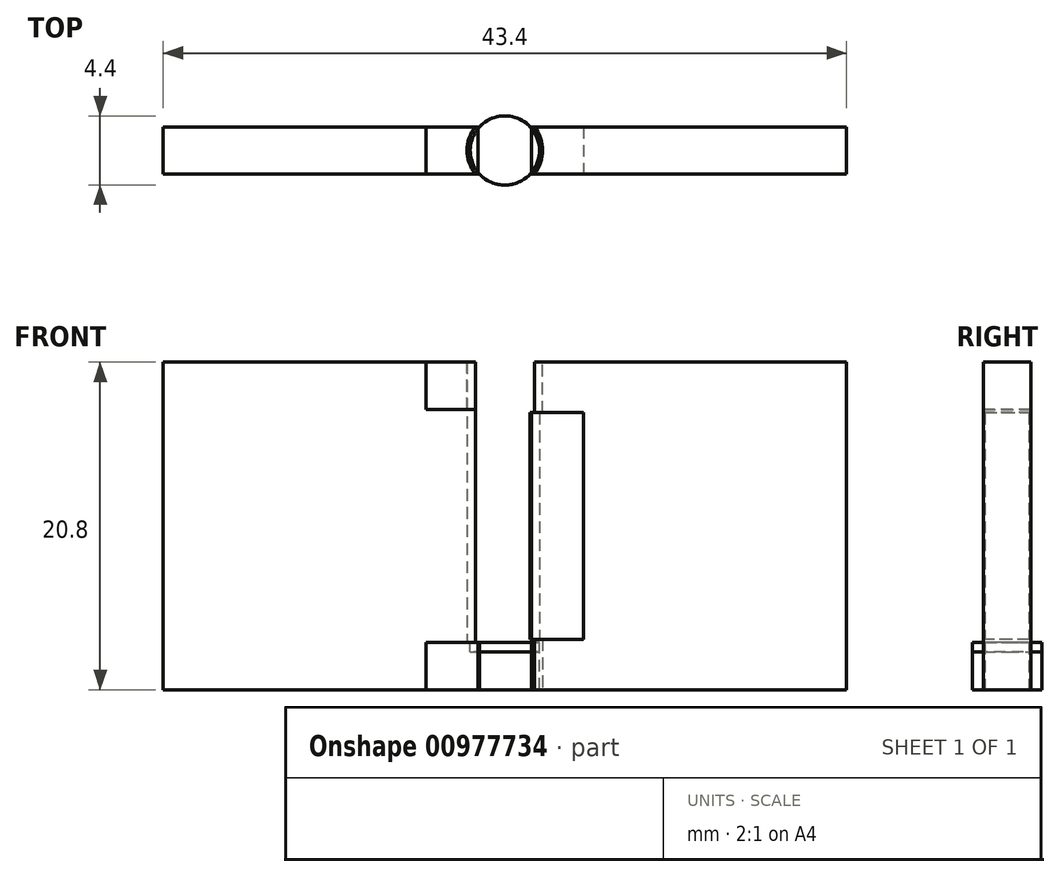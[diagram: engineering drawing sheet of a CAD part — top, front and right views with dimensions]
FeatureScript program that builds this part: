
annotation { "Feature Type Name" : "Feature", "Feature Type Description" : "" }
export const myFeature = defineFeature(function(context is Context, id is Id, definition is map)
    precondition{}
    {
        {
            var Q0;
            Q0=qCreatedBy(makeId("Front.planeOp"),FACE);
            var sketch = newSketch(context, id + "F0", { "sketchPlane" : qUnion([Q0])});
            skLineSegment(sketch, "E0", {"start": v(-1, 0.6) * mm, "end": v(-1, 2.6) * mm});
            skLineSegment(sketch, "E1", {"start": v(-1, 13.4) * mm, "end": v(-1, 15.4) * mm});
            skLineSegment(sketch, "E2", {"start": v(0, 20) * mm, "end": v(0, 0) * mm});
            skFitSpline(sketch, "E3", {"points": [v(-1, 13.4) * mm, v(-1, 2.6) * mm], "startDerivative": vector(2.12, -2.12) * mm, "endDerivative": vector(-2.12, -2.12) * mm});
            skLineSegment(sketch, "E4", {"start": v(-1, 13.4) * mm, "end": v(-0.3, 12.7) * mm, "construction": true});
            skLineSegment(sketch, "E5", {"start": v(-1, 2.6) * mm, "end": v(-0.3, 3.3) * mm, "construction": true});
            skLineSegment(sketch, "E6", {"start": v(-1.2, 15.2) * mm, "end": v(-1.2, 13.32) * mm});
            skLineSegment(sketch, "E7", {"start": v(-1.2, 2.68) * mm, "end": v(-1.2, 0.8) * mm});
            skFitSpline(sketch, "E8", {"points": [v(-1.2, 13.32) * mm, v(-1.2, 2.68) * mm], "startDerivative": vector(2.12, -2.12) * mm, "endDerivative": vector(-2.12, -2.12) * mm});
            skLineSegment(sketch, "E9", {"start": v(-1.2, 2.68) * mm, "end": v(-0.5, 3.39) * mm, "construction": true});
            skLineSegment(sketch, "E10", {"start": v(-1.2, 13.32) * mm, "end": v(-0.5, 12.61) * mm, "construction": true});
            skLineSegment(sketch, "E11", {"start": v(-1.2, 15.2) * mm, "end": v(-2.2, 15.2) * mm});
            skLineSegment(sketch, "E12", {"start": v(-2.2, 15.2) * mm, "end": v(-2.2, 0.8) * mm});
            skLineSegment(sketch, "E13", {"start": v(-2.2, 0.8) * mm, "end": v(-1.2, 0.8) * mm});
            skLineSegment(sketch, "E14", {"start": v(-1, 15.4) * mm, "end": v(-2.2, 15.4) * mm});
            skLineSegment(sketch, "E15", {"start": v(-2.2, 15.4) * mm, "end": v(-2.2, 16) * mm});
            skLineSegment(sketch, "E16", {"start": v(-2.2, 16) * mm, "end": v(0, 16) * mm});
            skLineSegment(sketch, "E17", {"start": v(0, 20) * mm, "end": v(0, 16) * mm});
            skLineSegment(sketch, "E18", {"start": v(-1, 0.6) * mm, "end": v(-2.2, 0.6) * mm});
            skLineSegment(sketch, "E19", {"start": v(-2.2, 0.6) * mm, "end": v(-2.2, 0) * mm});
            skLineSegment(sketch, "E20", {"start": v(-2.2, 0) * mm, "end": v(0, 0) * mm});
            skPoint(sketch, "E21", {"position": v(-2.2, 8) * mm});
            skSolve(sketch);
        }
        {
            var Q0;
            {Q0=qUnion([makeQuery(id+"F0.imprint","IMPRINT",FACE,{"disambiguationData":[TD([[makeQuery(id+"F0.imprint","IMPRINT",EDGE,{"derivedFrom":sQuery(id+"F0.wireOp",EDGE,"E0")}),-1.0]])]}),makeQuery(id+"F0.imprint","IMPRINT",FACE,{"disambiguationData":[TD([[makeQuery(id+"F0.imprint","IMPRINT",EDGE,{"derivedFrom":sQuery(id+"F0.wireOp",EDGE,"E6")}),-1.0]])]})]);}
            var Q1;
            Q1=sQuery(id+"F0.wireOp",EDGE,"E2");
            revolve(context, id + "F1", {"surfaceOperationType" : NewSurfaceOperationType.NEW, "entities" : qUnion([Q0]), "axis" : qUnion([Q1]), "revolveType" : RevolveType.FULL});
        }
        {
            var Q0;
            Q0=makeQuery(id+"F1.opRevolve","SWEPT_FACE",FACE,{"disambiguationData":[OSD([sQuery(id+"F0.wireOp",EDGE,"E14")])]});
            var sketch = newSketch(context, id + "F2", { "sketchPlane" : qUnion([Q0])});
            skCircle(sketch, "E22.0", {"center": v(0, 0) * mm, "radius": 2.2 * mm});
            skLineSegment(sketch, "E23", {"start": v(-5, -1.5) * mm, "end": v(-5, 1.5) * mm});
            skPoint(sketch, "E24", {"position": v(-5, 0) * mm});
            skLineSegment(sketch, "E25", {"start": v(-5, 1.5) * mm, "end": v(-1.6, 1.5) * mm});
            skLineSegment(sketch, "E26", {"start": v(-5, -1.5) * mm, "end": v(-1.6, -1.5) * mm});
            skSolve(sketch);
        }
        {
            var Q0;
            Q0=qSketchRegion(id+"F2",true);
            extrude(context, id + "F3", {"entities" : qUnion([Q0]), "oppositeDirection" : true, "depth" : 3 * mm, "offsetDistance" : 25 * mm});
        }
        {
            var Q0;
            Q0=sQuery(id+"F0.wireOp",EDGE,"E12");
            cPoint(context, id + "F4", {"entities" : qUnion([Q0]), "parameter" : 0.5});
        }
        {
            var Q0;
            Q0=qCreatedBy(id+"F4",VERTEX);
            var Q1;
            Q1=qCreatedBy(makeId("Top.planeOp"),FACE);
            cPlane(context, id + "F5", {"entities" : qUnion([Q0, Q1]), "cplaneType" : CPlaneType.PLANE_POINT, "offset" : 10 * mm, "oppositeDirection" : true, "width" : 150 * mm, "height" : 150 * mm});
        }
        {
            var Q0;
            Q0=makeQuery(id+"F3.opExtrude","SWEPT_BODY",BODY,{"disambiguationData":[OSD([sQuery(id+"F2.wireOp",EDGE,"E22.0"),sQuery(id+"F2.wireOp",EDGE,"TC6tmQ0S-Yqyp-8cfE-aPuB-eqh3s4vsYZ5D"),sQuery(id+"F2.wireOp",EDGE,"bjhKsaEG-cVOX-Fkbz-CbkF-KtJ3GnmFkV8B"),sQuery(id+"F2.wireOp",EDGE,"mCJQ4lcK-q60s-A4tl-M03E-BbWkXgAuEyKJ")])]});
            var Q1;
            Q1=qCreatedBy(id+"F5.planeOp",FACE);
            mirror(context, id + "F6", {"entities" : qUnion([Q0]), "mirrorPlane" : qUnion([Q1])});
        }
        {
            var Q0;
            Q0=makeQuery(id+"F1.opRevolve","SWEPT_FACE",FACE,{"disambiguationData":[OSD([sQuery(id+"F0.wireOp",EDGE,"E11")])]});
            var sketch = newSketch(context, id + "F7", { "sketchPlane" : qUnion([Q0])});
            skCircle(sketch, "E27.0.0", {"center": v(0, 0) * mm, "radius": 2.2 * mm});
            skCircle(sketch, "E28.0", {"center": v(0, 0) * mm, "radius": 1.2 * mm});
            skLineSegment(sketch, "E29", {"start": v(5, 1.5) * mm, "end": v(5, -1.5) * mm});
            skPoint(sketch, "E30", {"position": v(5, 0) * mm});
            skLineSegment(sketch, "E31", {"start": v(5, -1.5) * mm, "end": v(1.6, -1.5) * mm});
            skLineSegment(sketch, "E32", {"start": v(5, 1.5) * mm, "end": v(1.6, 1.5) * mm});
            skSolve(sketch);
        }
        {
            var Q0;
            Q0=makeQuery(id+"F7.imprint","IMPRINT",FACE,{"disambiguationData":[TD([[makeQuery(id+"F7.imprint","IMPRINT",EDGE,{"derivedFrom":sQuery(id+"F7.wireOp",EDGE,"E29")}),-1.0]])]});
            var Q1;
            Q1=qCreatedBy(id+"F5.planeOp",FACE);
            extrude(context, id + "F8", {"entities" : qUnion([Q0]), "endBound" : BoundingType.UP_TO_SURFACE, "oppositeDirection" : true, "depth" : 6 * mm, "endBoundEntityFace" : qUnion([Q1]), "offsetDistance" : 25 * mm});
        }
        {
            var Q0;
            Q0=makeQuery(id+"F8.opExtrude","SWEPT_BODY",BODY,{"disambiguationData":[OSD([sQuery(id+"F7.wireOp",EDGE,"E27.0.0"),sQuery(id+"F7.wireOp",EDGE,"IGmIIkr0-UC7I-SQ2f-CYrj-rGYYXajgl1JJ"),sQuery(id+"F7.wireOp",EDGE,"ZHcqityA-W586-mcKd-Iscn-xaArEYFfNkmQ"),sQuery(id+"F7.wireOp",EDGE,"cz0Gnaut-MDit-a28b-WmXf-ZYZsQhrKTzKM")])]});
            var Q1;
            Q1=qCreatedBy(id+"F5.planeOp",FACE);
            mirror(context, id + "F9", {"entities" : qUnion([Q0]), "mirrorPlane" : qUnion([Q1])});
        }
        {
            var Q0;
            Q0=makeQuery(id+"F1.opRevolve","SWEPT_BODY",BODY,{"disambiguationData":[OSD([sQuery(id+"F0.wireOp",EDGE,"E6"),sQuery(id+"F0.wireOp",EDGE,"E7"),sQuery(id+"F0.wireOp",EDGE,"E8"),sQuery(id+"F0.wireOp",EDGE,"E11"),sQuery(id+"F0.wireOp",EDGE,"E12"),sQuery(id+"F0.wireOp",EDGE,"E13")])]});
            var Q1;
            Q1=makeQuery(id+"F8.opExtrude","SWEPT_BODY",BODY,{"disambiguationData":[OSD([sQuery(id+"F7.wireOp",EDGE,"E27.0.0"),sQuery(id+"F7.wireOp",EDGE,"IGmIIkr0-UC7I-SQ2f-CYrj-rGYYXajgl1JJ"),sQuery(id+"F7.wireOp",EDGE,"ZHcqityA-W586-mcKd-Iscn-xaArEYFfNkmQ"),sQuery(id+"F7.wireOp",EDGE,"cz0Gnaut-MDit-a28b-WmXf-ZYZsQhrKTzKM")])]});
            var Q2;
            Q2=makeQuery(id+"F9.opPattern","COPY",BODY,{"derivedFrom":makeQuery(id+"F8.opExtrude","SWEPT_BODY",BODY,{"disambiguationData":[OSD([sQuery(id+"F7.wireOp",EDGE,"E27.0.0"),sQuery(id+"F7.wireOp",EDGE,"IGmIIkr0-UC7I-SQ2f-CYrj-rGYYXajgl1JJ"),sQuery(id+"F7.wireOp",EDGE,"ZHcqityA-W586-mcKd-Iscn-xaArEYFfNkmQ"),sQuery(id+"F7.wireOp",EDGE,"cz0Gnaut-MDit-a28b-WmXf-ZYZsQhrKTzKM")])]}),"instanceName":"1"});
            booleanBodies(context, id + "F10", {"operationType" : BooleanOperationType.UNION, "tools" : qUnion([Q0, Q1, Q2])});
        }
        {
            var Q0;
            Q0=qCreatedBy(makeId("Front.planeOp"),FACE);
            var sketch = newSketch(context, id + "F11", { "sketchPlane" : qUnion([Q0])});
            skLineSegment(sketch, "E33", {"start": v(-2.2, 0.8) * mm, "end": v(-2.2, 15.2) * mm});
            skLineSegment(sketch, "E34.bottom", {"start": v(-21.7, 18.4) * mm, "end": v(-1.7, 18.4) * mm});
            skLineSegment(sketch, "E34.top", {"start": v(-21.7, -2.4) * mm, "end": v(-1.7, -2.4) * mm});
            skLineSegment(sketch, "E34.left", {"start": v(-21.7, 18.4) * mm, "end": v(-21.7, -2.4) * mm});
            skLineSegment(sketch, "E34.right", {"start": v(-1.7, 18.4) * mm, "end": v(-1.7, -2.4) * mm});
            skLineSegment(sketch, "E35.bottom", {"start": v(21.7, 18.4) * mm, "end": v(1.7, 18.4) * mm});
            skLineSegment(sketch, "E35.top", {"start": v(21.7, -2.4) * mm, "end": v(1.7, -2.4) * mm});
            skLineSegment(sketch, "E35.left", {"start": v(21.7, 18.4) * mm, "end": v(21.7, -2.4) * mm});
            skLineSegment(sketch, "E35.right", {"start": v(1.7, 18.4) * mm, "end": v(1.7, -2.4) * mm});
            skLineSegment(sketch, "E36.0", {"start": v(-1.6, -2.4) * mm, "end": v(2.2, -2.4) * mm});
            skLineSegment(sketch, "E37.0", {"start": v(-1.6, 18.4) * mm, "end": v(2.2, 18.4) * mm});
            skLineSegment(sketch, "E38.MirrorCS", {"start": v(2.2, 0.8) * mm, "end": v(2.2, 15.2) * mm});
            skSolve(sketch);
        }
        {
            var Q0;
            Q0=qSketchRegion(id+"F11",true);
            extrude(context, id + "F12", {"entities" : qUnion([Q0]), "endBound" : BoundingType.SYMMETRIC, "depth" : 3 * mm, "offsetDistance" : 25 * mm});
        }
        {
            var Q0;
            Q0=makeQuery(id+"F12.opExtrude","SWEPT_FACE",FACE,{"disambiguationData":[OSD([sQuery(id+"F11.wireOp",EDGE,"E35.top")])]});
            var sketch = newSketch(context, id + "F13", { "sketchPlane" : qUnion([Q0])});
            skLineSegment(sketch, "E39.0", {"start": v(1.6, 1.5) * mm, "end": v(1.6, 1.5) * mm});
            skCircle(sketch, "E40", {"center": v(0, 0) * mm, "radius": 2.4 * mm});
            skArc(sketch, "E41.0", {"start": v(-1.6, 1.5) * mm, "mid": v(2.2, 0) * mm, "end": v(-1.6, -1.5) * mm});
            skSolve(sketch);
        }
        {
            var Q0;
            {var subQ0=sQuery(id+"F11.wireOp",EDGE,"E35.top");var subQ6=makeQuery(id+"F12.opExtrude","CAP_EDGE",EDGE,{"disambiguationData":[OSD([subQ0])],"isStart":true});var subQ9=sQuery(id+"F13.wireOp",EDGE,"E40");var subQ10=makeQuery(id+"F13.imprint","INTERSECT",VERTEX,{"derivedFrom":[subQ6,subQ9]});Q0=makeQuery(id+"F13.imprint","IMPRINT",FACE,{"disambiguationData":[TD([[makeQuery(id+"F13.imprint","IMPRINT",EDGE,{"disambiguationData":[TD([[subQ10,-1.0]])],"derivedFrom":subQ9}),1.0]])]});}
            var Q1;
            {var subQ0=sQuery(id+"F13.wireOp",EDGE,"ac114a6b-6946-46ee-80ea-92bb40bdf1b8.0");var subQ1=makeQuery(id+"F12.opExtrude","SWEPT_EDGE",EDGE,{"disambiguationData":[OSD([sQuery(id+"F11.wireOp",EDGE,"E35.top"),sQuery(id+"F11.wireOp",EDGE,"E35.right")])]});var subQ2=makeQuery(id+"F13.imprint","INTERSECT",VERTEX,{"disambiguationData":[OD(0.0)],"derivedFrom":[subQ1,subQ0]});Q1=makeQuery(id+"F13.imprint","IMPRINT",FACE,{"disambiguationData":[TD([[makeQuery(id+"F13.imprint","IMPRINT",EDGE,{"disambiguationData":[TD([[subQ2,-1.0]])],"derivedFrom":subQ0}),-1.0]])]});}
            var Q2;
            {var subQ0=sQuery(id+"F13.wireOp",EDGE,"E41.0");var subQ1=makeQuery(id+"F12.opExtrude","SWEPT_EDGE",EDGE,{"disambiguationData":[OSD([sQuery(id+"F11.wireOp",EDGE,"E35.right"),sQuery(id+"F11.wireOp",EDGE,"E36.0")])]});var subQ2=makeQuery(id+"F13.imprint","INTERSECT",VERTEX,{"disambiguationData":[OD(0.0)],"derivedFrom":[subQ1,subQ0]});Q2=makeQuery(id+"F13.imprint","IMPRINT",FACE,{"disambiguationData":[TD([[makeQuery(id+"F13.imprint","IMPRINT",EDGE,{"disambiguationData":[TD([[subQ2,1.0]])],"derivedFrom":subQ0}),-1.0]])]});}
            var Q3;
            Q3=makeQuery(id+"F10.opBoolean","MERGE",FACE,{"derivedFrom":[makeQuery(id+"F1.opRevolve","SWEPT_FACE",FACE,{"disambiguationData":[OSD([sQuery(id+"F0.wireOp",EDGE,"E13")])]}),makeQuery(id+"F9.opPattern","COPY",FACE,{"derivedFrom":makeQuery(id+"F8.opExtrude","CAP_FACE",FACE,{"disambiguationData":[OSD([sQuery(id+"F7.wireOp",EDGE,"E27.0.0"),sQuery(id+"F7.wireOp",EDGE,"E29"),sQuery(id+"F7.wireOp",EDGE,"E31"),sQuery(id+"F7.wireOp",EDGE,"E32")])],"isStart":true}),"instanceName":"1"})]});
            extrude(context, id + "F14", {"entities" : qUnion([Q0, Q1, Q2]), "operationType" : NewBodyOperationType.REMOVE, "endBound" : BoundingType.UP_TO_SURFACE, "oppositeDirection" : true, "depth" : 25 * mm, "endBoundEntityFace" : qUnion([Q3]), "offsetDistance" : 25 * mm});
        }
        {
            var Q0;
            Q0=makeQuery(id+"F6.opPattern","COPY",FACE,{"derivedFrom":makeQuery(id+"F3.opExtrude","CAP_FACE",FACE,{"disambiguationData":[OSD([sQuery(id+"F2.wireOp",EDGE,"E22.0"),sQuery(id+"F2.wireOp",EDGE,"E23"),sQuery(id+"F2.wireOp",EDGE,"7c0a10cd-0586-4f9a-8963-d188ea9eb1bb"),sQuery(id+"F2.wireOp",EDGE,"9f79ce4d-a61a-416a-865d-89767d7a2cce")])],"isStart":true}),"instanceName":"1"});
            var sketch = newSketch(context, id + "F15", { "sketchPlane" : qUnion([Q0])});
            skLineSegment(sketch, "E42.0", {"start": v(1.6, -1.5) * mm, "end": v(1.6, -1.5) * mm});
            skCircle(sketch, "E43", {"center": v(0, 0) * mm, "radius": 2.4 * mm});
            skSolve(sketch);
        }
        {
            var Q0;
            {var subQ1=makeQuery(id+"F6.opPattern","COPY",EDGE,{"derivedFrom":makeQuery(id+"F3.opExtrude","CAP_EDGE",EDGE,{"disambiguationData":[OSD([sQuery(id+"F2.wireOp",EDGE,"E22.0")])],"isStart":true}),"instanceName":"1"});Q0=makeQuery(id+"F15.imprint","IMPRINT",FACE,{"disambiguationData":[TD([[makeQuery(id+"F15.imprint","IMPRINT",EDGE,{"derivedFrom":subQ1}),1.0]])]});}
            var Q1;
            Q1=makeQuery(id+"F3.opExtrude","CAP_FACE",FACE,{"disambiguationData":[OSD([sQuery(id+"F2.wireOp",EDGE,"E22.0"),sQuery(id+"F2.wireOp",EDGE,"E23"),sQuery(id+"F2.wireOp",EDGE,"7c0a10cd-0586-4f9a-8963-d188ea9eb1bb"),sQuery(id+"F2.wireOp",EDGE,"9f79ce4d-a61a-416a-865d-89767d7a2cce")])],"isStart":true});
            extrude(context, id + "F16", {"entities" : qUnion([Q0]), "operationType" : NewBodyOperationType.REMOVE, "endBound" : BoundingType.UP_TO_SURFACE, "depth" : 25 * mm, "endBoundEntityFace" : qUnion([Q1]), "offsetDistance" : 25 * mm});
        }
        {
            var Q0;
            Q0=makeQuery(id+"F12.opExtrude","SWEPT_FACE",FACE,{"disambiguationData":[OSD([sQuery(id+"F11.wireOp",EDGE,"E35.bottom")])]});
            var sketch = newSketch(context, id + "F17", { "sketchPlane" : qUnion([Q0])});
            skLineSegment(sketch, "E44.0", {"start": v(1.6, -1.5) * mm, "end": v(1.6, -1.5) * mm});
            skCircle(sketch, "E45", {"center": v(0, 0) * mm, "radius": 2.4 * mm});
            skSolve(sketch);
        }
        {
            var Q0;
            Q0 = qSketchRegion(id + "F17", true);
            var Q1;
            Q1=makeQuery(id+"F10.opBoolean","MERGE",FACE,{"derivedFrom":[makeQuery(id+"F1.opRevolve","SWEPT_FACE",FACE,{"disambiguationData":[OSD([sQuery(id+"F0.wireOp",EDGE,"E11")])]}),makeQuery(id+"F8.opExtrude","CAP_FACE",FACE,{"disambiguationData":[OSD([sQuery(id+"F7.wireOp",EDGE,"E27.0.0"),sQuery(id+"F7.wireOp",EDGE,"E29"),sQuery(id+"F7.wireOp",EDGE,"E31"),sQuery(id+"F7.wireOp",EDGE,"E32")])],"isStart":true})]});
            extrude(context, id + "F18", {"entities" : qUnion([Q0]), "operationType" : NewBodyOperationType.REMOVE, "endBound" : BoundingType.UP_TO_SURFACE, "oppositeDirection" : true, "depth" : 25 * mm, "endBoundEntityFace" : qUnion([Q1]), "offsetDistance" : 25 * mm});
        }
    });
